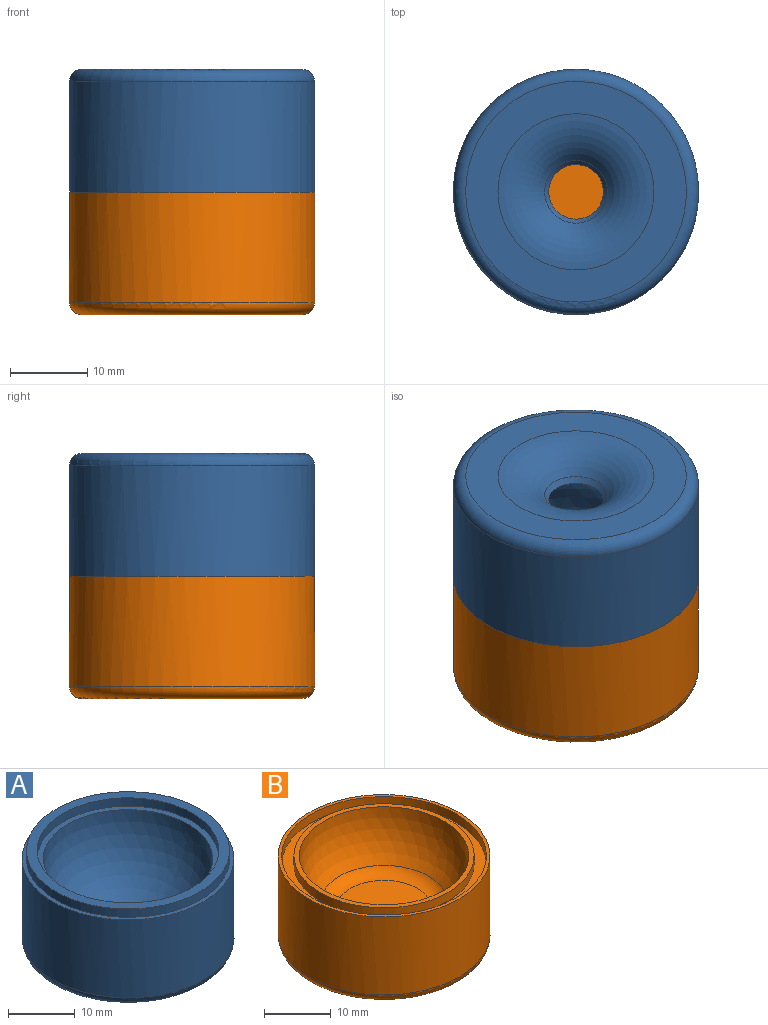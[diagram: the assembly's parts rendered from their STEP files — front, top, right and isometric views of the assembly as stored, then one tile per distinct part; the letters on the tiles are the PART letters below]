
ASSEMBLY  parts=2 mates=1
PART A: 11 faces, bbox 34.4x34.4x17.4 mm
  f0: plane 31.75x31.75mm, normal (0,0,1), area 65.3mm2, adj f1,f4
  f1: cylinder r=15.88mm len=31.75mm, axis (0,0,1), area 1425.1mm2, adj f0,f10
  f2: plane 28.58x28.58mm, normal (0,0,-1), area 320.3mm2, adj f9,f10
  f3: cylinder r=13.62mm len=27.24mm, axis (0,0,-1), area 130.4mm2, adj f5,f7
  f4: cylinder r=15.21mm len=30.41mm, axis (0,0,-1), area 145.6mm2, adj f0,f5
  f5: plane 30.41x30.41mm, normal (0,0,1), area 143.8mm2, adj f3,f4
  f6: sphere r=12.7mm, area 973.5mm2, adj f7,f8
  f7: plane 27.24x27.24mm, normal (0,0,1), area 76mm2, adj f3,f6
  f8: cone r=6.35mm half-angle=37.5deg, axis (0,0,-1), area 20.9mm2, adj f6,f9
  f9: torus R=10.11mm, axis (0,0,-1), area 300.7mm2, adj f2,f8
  f10: torus R=14.29mm, axis (0,0,-1), area 239.7mm2, adj f1,f2
PART B: 11 faces, bbox 34.4x34.4x15.9 mm
  f0: plane 26.99x26.99mm, normal (0,0,1), area 65.3mm2, adj f1,f4
  f1: sphere r=12.7mm, area 675.6mm2, adj f0,f3
  f2: plane 14.2x14.2mm, normal (0,0,1), area 158.3mm2, adj f3
  f3: torus R=7.1mm, axis (0,0,-1), area 140.2mm2, adj f1,f2
  f4: cylinder r=13.49mm len=26.99mm, axis (0,0,1), area 134.6mm2, adj f0,f6
  f5: cylinder r=15.33mm len=30.66mm, axis (0,0,1), area 152.9mm2, adj f6,f9
  f6: plane 30.66x30.66mm, normal (0,0,1), area 166.4mm2, adj f4,f5
  f7: plane 28.58x28.58mm, normal (0,0,-1), area 641.3mm2, adj f10
  f8: cylinder r=15.88mm len=31.75mm, axis (0,0,1), area 1425.1mm2, adj f9,f10
  f9: plane 31.75x31.75mm, normal (0,0,1), area 53.3mm2, adj f5,f8
  f10: torus R=14.29mm, axis (0,0,-1), area 239.7mm2, adj f7,f8
PLACE A rot(axis=(1,0,0),180deg) t=(31.63,15.3,3.43)mm
PLACE B t=(31.63,15.3,3.43)mm
MATE fastened A.f1 <-> B.f5  axis (0,0,-1) through (31.63,15.3,1.9)mm
